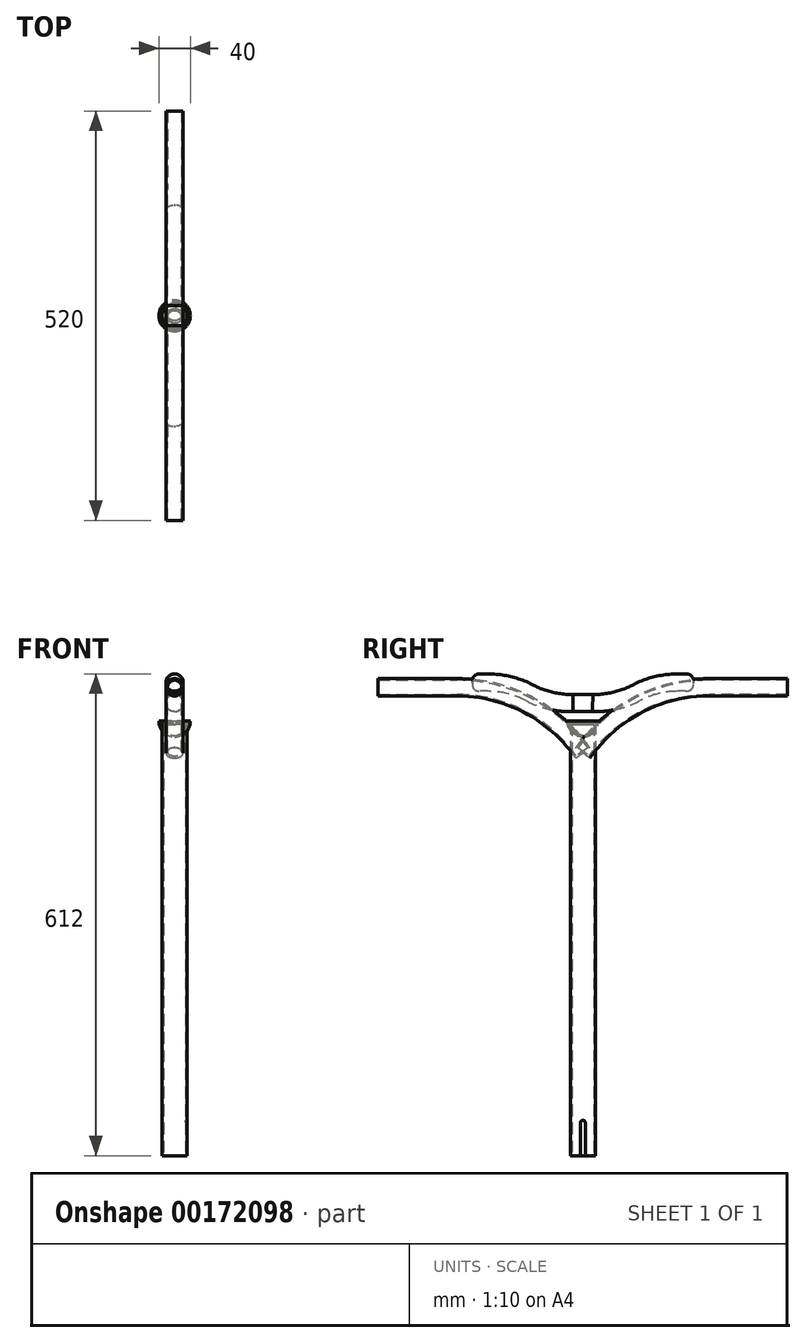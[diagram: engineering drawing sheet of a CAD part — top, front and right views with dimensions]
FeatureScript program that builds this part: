
annotation { "Feature Type Name" : "Feature", "Feature Type Description" : "" }
export const myFeature = defineFeature(function(context is Context, id is Id, definition is map)
    precondition{}
    {
        {
            var Q0;
            Q0=qCreatedBy(makeId("Top.planeOp"),FACE);
            var sketch = newSketch(context, id + "F0", { "sketchPlane" : qUnion([Q0])});
            skCircle(sketch, "E0", {"center": v(0, 0) * mm, "radius": 16 * mm});
            skSolve(sketch);
        }
        {
            var Q0;
            Q0 = qSketchRegion(id + "F0", true);
            extrude(context, id + "F1", {"entities" : qUnion([Q0]), "depth" : 550 * mm});
        }
        {
            var Q0;
            Q0=makeQuery(id+"F1.opExtrude","CAP_FACE",FACE,{"disambiguationData":[OSD([sQuery(id+"F0.wireOp",EDGE,"E0")])],"isStart":true});
            shell(context, id + "F2", {"entities" : qUnion([Q0]), "thickness" : 2 * mm});
        }
        {
            var Q0;
            Q0=qCreatedBy(makeId("Right.planeOp"),FACE);
            var sketch = newSketch(context, id + "F3", { "sketchPlane" : qUnion([Q0])});
            skLineSegment(sketch, "E1.bottom", {"start": v(-3, 0) * mm, "end": v(3, 0) * mm});
            skLineSegment(sketch, "E1.top", {"start": v(0, 45) * mm, "end": v(0, 45) * mm});
            skLineSegment(sketch, "E1.left", {"start": v(-3, 0) * mm, "end": v(-3, 42) * mm});
            skLineSegment(sketch, "E1.right", {"start": v(3, 0) * mm, "end": v(3, 42) * mm});
            skPoint(sketch, "E2.visualSharp", {"position": v(-3, 45) * mm});
            skArc(sketch, "E2.filletArc", {"start": v(0, 45) * mm, "mid": v(-2.12, 44.12) * mm, "end": v(-3, 42) * mm});
            skPoint(sketch, "E3.visualSharp", {"position": v(3, 45) * mm});
            skArc(sketch, "E3.filletArc", {"start": v(3, 42) * mm, "mid": v(2.12, 44.12) * mm, "end": v(0, 45) * mm});
            skSolve(sketch);
        }
        {
            var Q0;
            Q0 = qSketchRegion(id + "F3", true);
            extrude(context, id + "F4", {"entities" : qUnion([Q0]), "operationType" : NewBodyOperationType.REMOVE, "endBound" : BoundingType.THROUGH_ALL, "depth" : 25 * mm});
        }
        {
            var Q0;
            Q0=qCreatedBy(makeId("Right.planeOp"),FACE);
            var sketch = newSketch(context, id + "F5", { "sketchPlane" : qUnion([Q0])});
            skArc(sketch, "E4", {"start": v(160, 595) * mm, "mid": v(69.75, 572.86) * mm, "end": v(0, 511.47) * mm});
            skLineSegment(sketch, "E5", {"start": v(160, 595) * mm, "end": v(260, 595) * mm});
            skSolve(sketch);
        }
        {
            var Q0;
            Q0=sQuery(id+"F5.wireOp",VERTEX,"E5.end");
            var Q1;
            Q1=qCreatedBy(makeId("Front.planeOp"),FACE);
            cPlane(context, id + "F6", {"entities" : qUnion([Q0, Q1]), "cplaneType" : CPlaneType.PLANE_POINT, "offset" : 25 * mm, "width" : 150 * mm, "height" : 150 * mm});
        }
        {
            var Q0;
            Q0=qCreatedBy(id+"F6.planeOp",FACE);
            var sketch = newSketch(context, id + "F7", { "sketchPlane" : qUnion([Q0])});
            skCircle(sketch, "E6", {"center": v(0, 595) * mm, "radius": 11 * mm});
            skSolve(sketch);
        }
        {
            var Q0;
            Q0 = qSketchRegion(id + "F7", true);
            var Q1;
            Q1 = qConstructionFilter(qBodyType(qCreatedBy(id + "F5" ,EDGE), BodyType.WIRE), ConstructionObject.NO);
            sweep(context, id + "F8", {"profiles" : qUnion([Q0]), "path" : qUnion([Q1])});
        }
        {
            var Q0;
            Q0=makeQuery(id+"F8.opSweep","CAP_FACE",FACE,{"disambiguationData":[OSD([sQuery(id+"F5.wireOp",VERTEX,"E5.end"),sQuery(id+"F7.wireOp",EDGE,"E6")])],"isStart":true});
            shell(context, id + "F9", {"entities" : qUnion([Q0]), "thickness" : 2 * mm});
        }
        {
            var Q0;
            Q0=makeQuery(id+"F8.opSweep","SWEPT_BODY",BODY,{"disambiguationData":[OSD([sQuery(id+"F5.wireOp",EDGE,"E5"),sQuery(id+"F7.wireOp",EDGE,"E6")])]});
            var Q1;
            Q1=qCreatedBy(makeId("Front.planeOp"),FACE);
            mirror(context, id + "F10", {"entities" : qUnion([Q0]), "mirrorPlane" : qUnion([Q1])});
        }
        {
            var Q0;
            Q0=qCreatedBy(makeId("Right.planeOp"),FACE);
            var sketch = newSketch(context, id + "F11", { "sketchPlane" : qUnion([Q0])});
            skLineSegment(sketch, "E7", {"start": v(0, 0) * mm, "end": v(0, 196.68) * mm, "construction": true});
            skLineSegment(sketch, "E8", {"start": v(0, 575) * mm, "end": v(-12.5, 575) * mm});
            skLineSegment(sketch, "E9", {"start": v(-120.5, 601) * mm, "end": v(-140.5, 601) * mm});
            skArc(sketch, "E10", {"start": v(-67.38, 587.87) * mm, "mid": v(-93.14, 597.67) * mm, "end": v(-120.5, 601) * mm});
            skArc(sketch, "E11", {"start": v(-67.38, 587.87) * mm, "mid": v(-40.76, 577.93) * mm, "end": v(-12.5, 575) * mm});
            skLineSegment(sketch, "E12.MirrorCS", {"start": v(0, 575) * mm, "end": v(12.5, 575) * mm});
            skArc(sketch, "E13.MirrorCS", {"start": v(67.38, 587.87) * mm, "mid": v(40.76, 577.93) * mm, "end": v(12.5, 575) * mm});
            skArc(sketch, "E14.MirrorCS", {"start": v(67.38, 587.87) * mm, "mid": v(93.14, 597.67) * mm, "end": v(120.5, 601) * mm});
            skLineSegment(sketch, "E15.MirrorCS", {"start": v(120.5, 601) * mm, "end": v(140.5, 601) * mm});
            skSolve(sketch);
        }
        {
            var Q0;
            Q0=sQuery(id+"F11.wireOp",VERTEX,"E15.MirrorCS.end");
            var Q1;
            Q1=qCreatedBy(id+"F6.planeOp",FACE);
            cPlane(context, id + "F12", {"entities" : qUnion([Q0, Q1]), "cplaneType" : CPlaneType.PLANE_POINT, "offset" : 25 * mm, "width" : 150 * mm, "height" : 150 * mm});
        }
        {
            var Q0;
            Q0=qCreatedBy(id+"F12.planeOp",FACE);
            var sketch = newSketch(context, id + "F13", { "sketchPlane" : qUnion([Q0])});
            skCircle(sketch, "E16", {"center": v(0, 601) * mm, "radius": 11 * mm});
            skSolve(sketch);
        }
        {
            var Q0;
            Q0=makeQuery(id+"F13.imprint","IMPRINT",FACE,{"disambiguationData":[TD([[makeQuery(id+"F13.imprint","IMPRINT",EDGE,{"derivedFrom":sQuery(id+"F13.wireOp",EDGE,"E16")}),1.0]])]});
            var Q1;
            Q1 = qConstructionFilter(qBodyType(qCreatedBy(id + "F11" ,EDGE), BodyType.WIRE), ConstructionObject.NO);
            sweep(context, id + "F14", {"profiles" : qUnion([Q0]), "path" : qUnion([Q1])});
        }
        {
            var Q0;
            Q0=makeQuery(id+"F14.opSweep","CAP_FACE",FACE,{"disambiguationData":[OSD([sQuery(id+"F11.wireOp",VERTEX,"E9.end"),sQuery(id+"F13.wireOp",EDGE,"E16")])],"isStart":false});
            var Q1;
            Q1=makeQuery(id+"F14.opSweep","CAP_FACE",FACE,{"disambiguationData":[OSD([sQuery(id+"F11.wireOp",VERTEX,"E15.MirrorCS.end"),sQuery(id+"F13.wireOp",EDGE,"E16")])],"isStart":true});
            fillet(context, id + "F15", {"entities" : qUnion([Q0, Q1]), "radius" : 10 * mm, "tangentPropagation" : true, "rho" : .5, "crossSection" : FilletCrossSection.CONIC, "allowEdgeOverflow" : false});
        }
        {
            var Q0;
            Q0=qCreatedBy(makeId("Right.planeOp"),FACE);
            var sketch = newSketch(context, id + "F16", { "sketchPlane" : qUnion([Q0])});
            skArc(sketch, "E17", {"start": v(-20, 552) * mm, "mid": v(-14.14, 537.86) * mm, "end": v(0, 532) * mm});
            skLineSegment(sketch, "E18", {"start": v(0, 552) * mm, "end": v(-20, 552) * mm});
            skLineSegment(sketch, "E19", {"start": v(0, 552) * mm, "end": v(0, 532) * mm});
            skSolve(sketch);
        }
        {
            var Q0;
            Q0 = qSketchRegion(id + "F16", true);
            var Q1;
            Q1=sQuery(id+"F16.wireOp",EDGE,"E19");
            revolve(context, id + "F17", {"entities" : qUnion([Q0]), "axis" : qUnion([Q1]), "revolveType" : RevolveType.FULL});
        }
        {
            var Q0;
            Q0=makeQuery(id+"F17.opRevolve","SWEPT_FACE",FACE,{"disambiguationData":[OSD([sQuery(id+"F16.wireOp",EDGE,"E18")])]});
            shell(context, id + "F18", {"entities" : qUnion([Q0]), "thickness" : 2 * mm});
        }
    });
